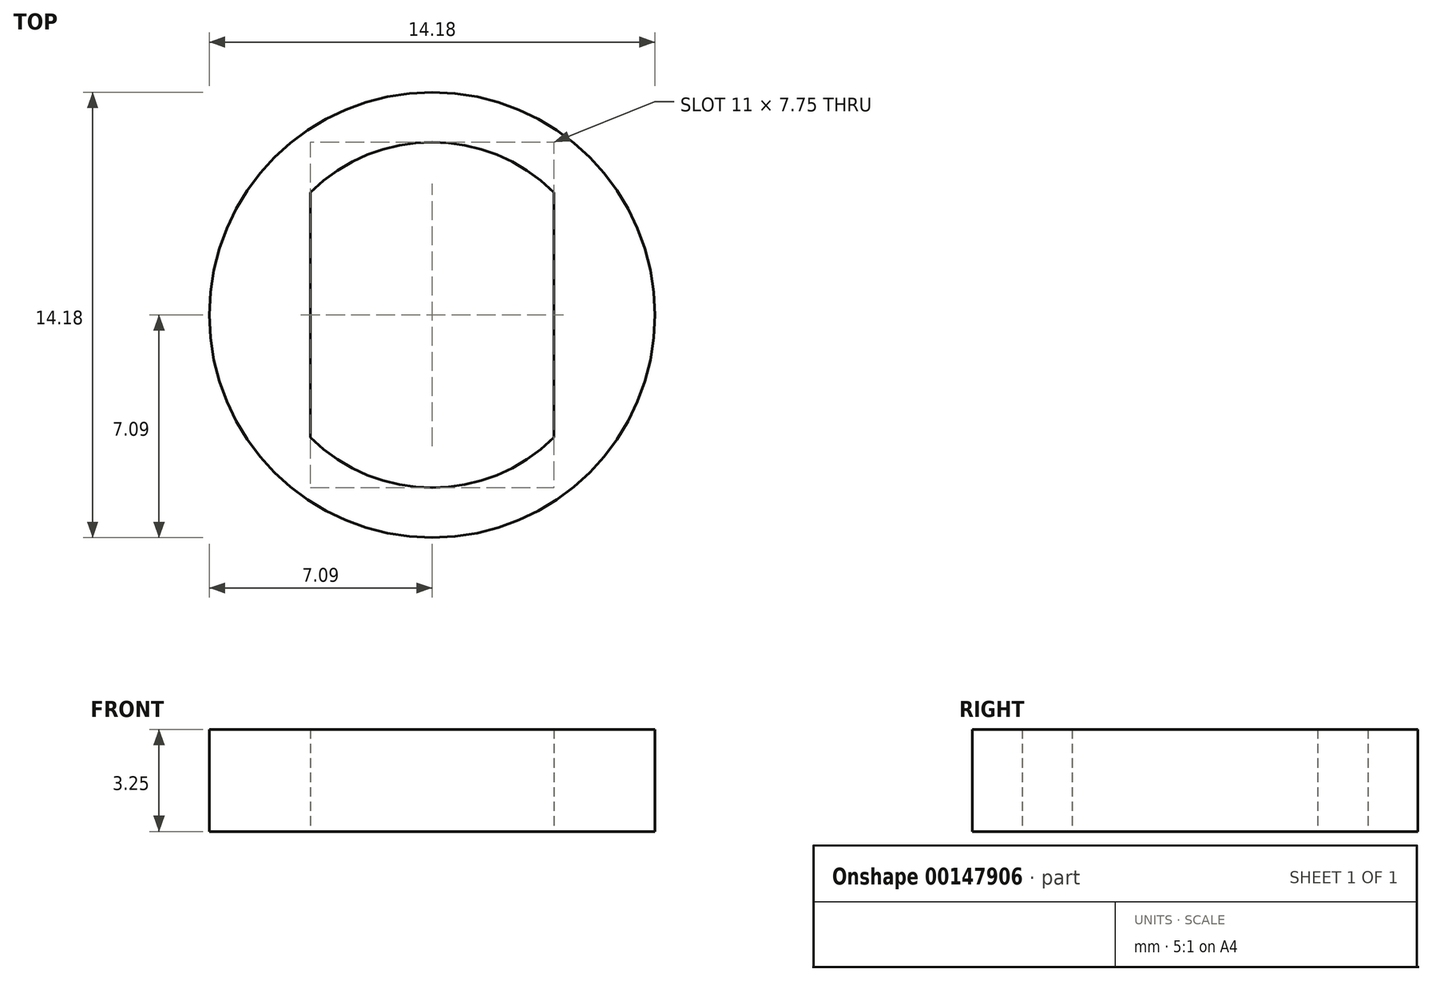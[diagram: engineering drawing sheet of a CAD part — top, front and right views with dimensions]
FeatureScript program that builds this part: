
annotation { "Feature Type Name" : "Feature", "Feature Type Description" : "" }
export const myFeature = defineFeature(function(context is Context, id is Id, definition is map)
    precondition{}
    {
        {
            var Q0;
            Q0=qCreatedBy(makeId("Top.planeOp"),FACE);
            var sketch = newSketch(context, id + "F0", { "sketchPlane" : qUnion([Q0])});
            skLineSegment(sketch, "E0.bottom", {"start": v(-3.87, -3.9) * mm, "end": v(3.87, -3.9) * mm, "construction": true});
            skLineSegment(sketch, "E0.top", {"start": v(-3.87, 3.9) * mm, "end": v(3.87, 3.9) * mm, "construction": true});
            skLineSegment(sketch, "E0.left", {"start": v(-3.87, -3.9) * mm, "end": v(-3.87, 3.9) * mm});
            skLineSegment(sketch, "E0.right", {"start": v(3.87, -3.9) * mm, "end": v(3.87, 3.9) * mm});
            skPoint(sketch, "E0.middle", {"position": v(0, 0) * mm});
            skArc(sketch, "E1", {"start": v(3.87, 3.9) * mm, "mid": v(0, 5.5) * mm, "end": v(-3.87, 3.9) * mm});
            skArc(sketch, "E2", {"start": v(-3.87, -3.9) * mm, "mid": v(0, -5.5) * mm, "end": v(3.87, -3.9) * mm});
            skCircle(sketch, "E3", {"center": v(0, 0) * mm, "radius": 7.09 * mm});
            skSolve(sketch);
        }
        {
            var Q0;
            Q0=makeQuery(id+"F0.imprint","IMPRINT",FACE,{"disambiguationData":[TD([[makeQuery(id+"F0.imprint","IMPRINT",EDGE,{"derivedFrom":sQuery(id+"F0.wireOp",EDGE,"E0.left")}),1.0]])]});
            extrude(context, id + "F1", {"entities" : qUnion([Q0]), "depth" : 3.25 * mm});
        }
    });
